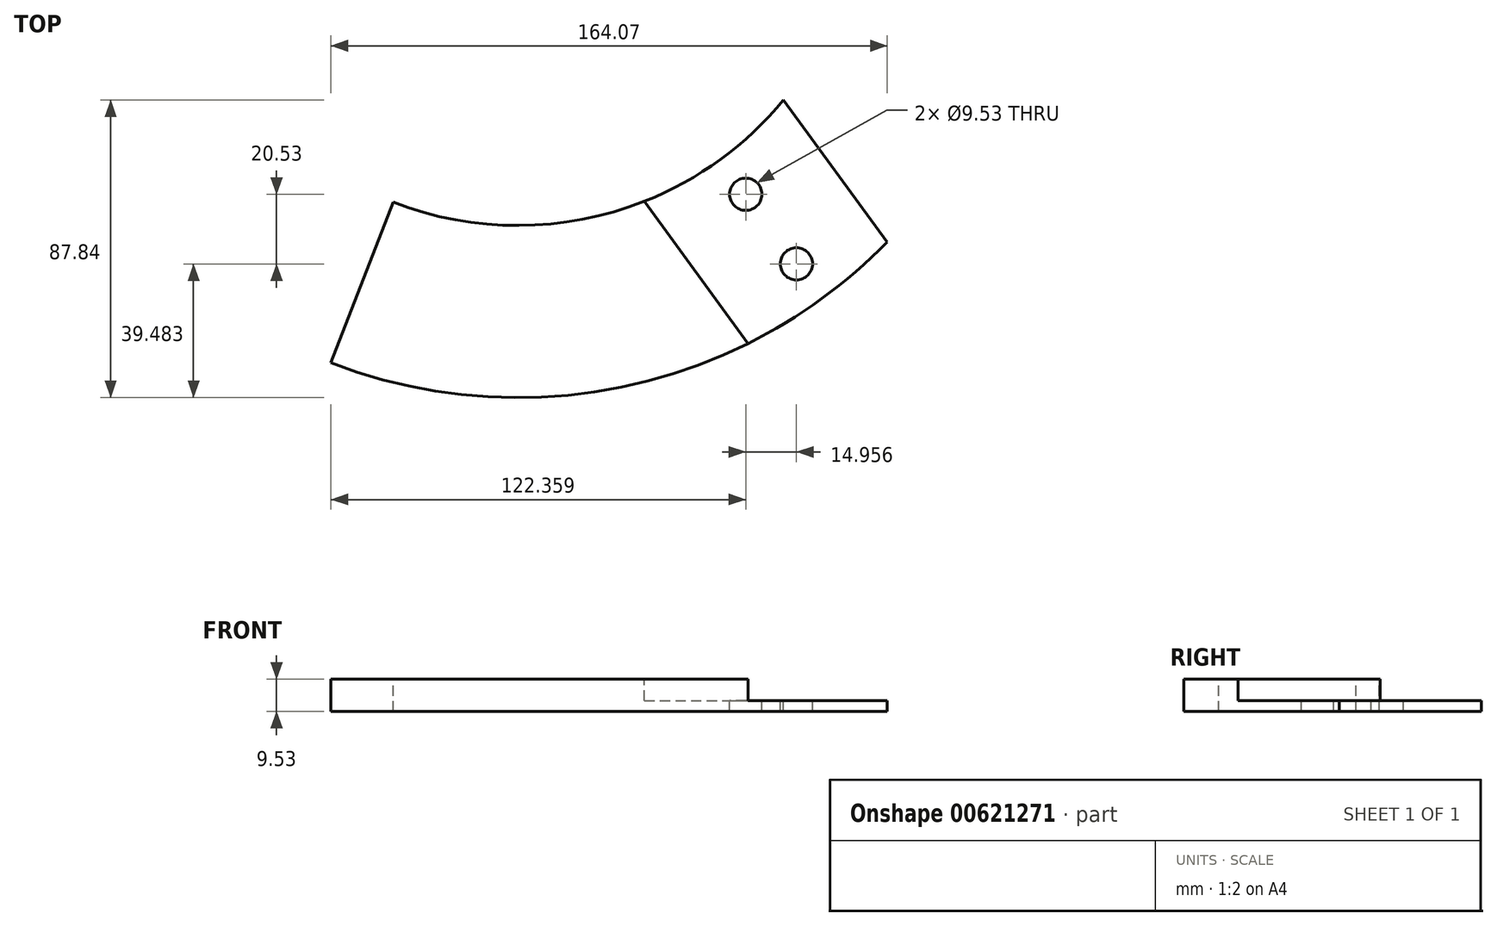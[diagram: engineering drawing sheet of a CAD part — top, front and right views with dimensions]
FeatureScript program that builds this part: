
annotation { "Feature Type Name" : "Feature", "Feature Type Description" : "" }
export const myFeature = defineFeature(function(context is Context, id is Id, definition is map)
    precondition{}
    {
        {
            var Q0;
            Q0=qCreatedBy(makeId("Top.planeOp"),FACE);
            var sketch = newSketch(context, id + "F0", { "sketchPlane" : qUnion([Q0])});
            skCircle(sketch, "E0", {"center": v(0, 0) * mm, "radius": 76.2 * mm});
            skCircle(sketch, "E1", {"center": v(0, 0) * mm, "radius": 101.6 * mm});
            skLineSegment(sketch, "E2", {"start": v(0, 0) * mm, "end": v(89.73, -123.18) * mm});
            skLineSegment(sketch, "E3.0", {"start": v(-20.53, -14.96) * mm, "end": v(67.95, -136.41) * mm});
            skLineSegment(sketch, "E4.0", {"start": v(20.53, 14.96) * mm, "end": v(109, -106.5) * mm});
            skArc(sketch, "E5", {"start": v(-55.06, -142.1) * mm, "mid": v(32.32, -148.93) * mm, "end": v(109, -106.5) * mm});
            skLineSegment(sketch, "E6", {"start": v(-36.7, -94.74) * mm, "end": v(-55.06, -142.1) * mm});
            skLineSegment(sketch, "E7", {"start": v(-20.53, -14.96) * mm, "end": v(20.53, 14.96) * mm});
            skCircle(sketch, "E8", {"center": v(67.3, -92.39) * mm, "radius": 4.76 * mm});
            skCircle(sketch, "E9", {"center": v(82.25, -112.92) * mm, "radius": 4.76 * mm});
            skSolve(sketch);
        }
        {
            var Q0;
            {var subQ0=sQuery(id+"F0.wireOp",EDGE,"E4.0");var subQ1=sQuery(id+"F0.wireOp",EDGE,"E1");var subQ2=makeQuery(id+"F0.imprint","INTERSECT",VERTEX,{"derivedFrom":[subQ1,subQ0]});Q0=makeQuery(id+"F0.imprint","IMPRINT",FACE,{"disambiguationData":[TD([[makeQuery(id+"F0.imprint","IMPRINT",EDGE,{"disambiguationData":[TD([[subQ2,1.0]])],"derivedFrom":subQ1}),-1.0]])]});}
            var Q1;
            {var subQ0=sQuery(id+"F0.wireOp",EDGE,"E3.0");var subQ1=sQuery(id+"F0.wireOp",EDGE,"E1");var subQ2=makeQuery(id+"F0.imprint","INTERSECT",VERTEX,{"derivedFrom":[subQ1,subQ0]});Q1=makeQuery(id+"F0.imprint","IMPRINT",FACE,{"disambiguationData":[TD([[makeQuery(id+"F0.imprint","IMPRINT",EDGE,{"disambiguationData":[TD([[subQ2,-1.0]])],"derivedFrom":subQ1}),-1.0]])]});}
            var Q2;
            {var subQ0=sQuery(id+"F0.wireOp",EDGE,"E6");Q2=makeQuery(id+"F0.imprint","IMPRINT",FACE,{"disambiguationData":[TD([[makeQuery(id+"F0.imprint","IMPRINT",EDGE,{"derivedFrom":subQ0}),1.0]])]});}
            extrude(context, id + "F1", {"entities" : qUnion([Q0, Q1, Q2]), "oppositeDirection" : true, "depth" : 9.52 * mm, "offsetDistance" : 25.4 * mm});
        }
        {
            var Q0;
            {var subQ0=sQuery(id+"F0.wireOp",EDGE,"E3.0");var subQ1=sQuery(id+"F0.wireOp",EDGE,"E1");var subQ2=makeQuery(id+"F0.imprint","INTERSECT",VERTEX,{"derivedFrom":[subQ1,subQ0]});Q0=makeQuery(id+"F0.imprint","IMPRINT",FACE,{"disambiguationData":[TD([[makeQuery(id+"F0.imprint","IMPRINT",EDGE,{"disambiguationData":[TD([[subQ2,-1.0]])],"derivedFrom":subQ1}),-1.0]])]});}
            var Q1;
            {var subQ0=sQuery(id+"F0.wireOp",EDGE,"E4.0");var subQ1=sQuery(id+"F0.wireOp",EDGE,"E1");var subQ2=makeQuery(id+"F0.imprint","INTERSECT",VERTEX,{"derivedFrom":[subQ1,subQ0]});Q1=makeQuery(id+"F0.imprint","IMPRINT",FACE,{"disambiguationData":[TD([[makeQuery(id+"F0.imprint","IMPRINT",EDGE,{"disambiguationData":[TD([[subQ2,1.0]])],"derivedFrom":subQ1}),-1.0]])]});}
            extrude(context, id + "F2", {"entities" : qUnion([Q0, Q1]), "operationType" : NewBodyOperationType.REMOVE, "oppositeDirection" : true, "depth" : 6.35 * mm, "offsetDistance" : 25.4 * mm});
        }
    });
